# Revit family: LEGRAND_NON INTERLOCKED SOCKETS_SURFACE MOUNTED_IP44_230
name_source: partatom
category: Installations électriques
revit_build: Autodesk Revit 2018 (Build: 20170223_1515(x64)
units: mm (PartAtom-declared; Revit-internal decimal feet)

## family parameters
Conserver l'orientation des annotations = Non
Cote de connecteur circulaire = Utiliser le diamètre
Couper avec des vides une fois chargée = Non
Hôte = Face
Partagée = Non
Point de calcul de pièce = Non
Type d'élément = Normal

## types (19) — shared parameters
Description = international standard socket for flush or surface mounting with accessory allows the connection of power devices
Dia bouchon = 50 mm  [stored 0.164042 ft]
Elévation par défaut = 1000 mm  [stored 3.28084 ft]
Fabricant = Legrand
Flush E or Surface mounting S = flush and surface mounting
General Conditions of Use = https://export.legrand.com
Maximum installation temperature = 40°C
Maximum use temperature = 100°C
Minimum installation temperature = -20°C
Minimum use temperature = -50°C
RAY BOUCHON = 25 mm  [stored 0.082021 ft]
Ray = 25 mm  [stored 0.082021 ft]
Standard IEC or NFC = IEC
Tension V = 230 V  50/60 Hz blue
characteristic color = blue
connecting type = screw terminals
protection class IP = IP44

## per-type parameters (varying)
| type | Modèle | Number of poles | Position of earth h | depth for flush mounting mm | depth mm | h1 | halogen free | height mm | horizontal fixing distance mm | intensity A | material of box | resistance to chocks IK | vertical fixing distance mm | width mm |
| panel mounting socket Hypra   IP44   16 A   200/250 V   2P+E   plast surface box for passage wiring | 052022 | 3 | 6 | 75 mm | 115 mm | 109 mm | Oui | 182 mm | 52 mm | 16 A | plastic | 09 | 60 mm | 86 mm |
| panel mounting socket Hypra   IP44   16 A   200/250 V   3P+E   plast surface box for passage wiring | 052023 | 4 | 9 | 77 mm | 117 mm | 127 mm | Oui | 212 mm | 60 mm | 16 A | plastic | 09 | 70 mm | 100 mm  [stored 0.328084 ft] |
| panel mounting socket Hypra   IP44   16 A   200/250 V   3P+N+E   plast surface box for passage wiring | 052024 | 5 | 9 | 77 mm | 121 mm | 127 mm | Oui | 212 mm | 60 mm | 16 A | plastic | 09 | 70 mm | 100 mm  [stored 0.328084 ft] |
| panel mounting socket Hypra   IP44   16 A   200/250 V   2P+E   métal surface mounting | 052032 | 3 | 6 | 58 mm | 98 mm | 64 mm | Oui | 106 mm | 52 mm | 16 A | metal | 10 | 60 mm | 74 mm |
| panel mounting socket Hypra   IP44   16 A   200/250 V   3P+N+E   métal surface mounting | 052034 | 5 | 9 | 60 mm | 104 mm | 73 mm | Oui | 122 mm  [stored 0.400262 ft] | 60 mm | 16 A | metal | 10 | 70 mm | 96 mm |
| panel mounting socket Hypra   IP44   32 A   200/250 V   2P+E   plast surface box for passage wiring | 052718 | 3 | 6 | 90 mm | 143 mm | 97 mm | Oui | 162 mm | 70 mm | 32 A | plastic | 09 | 70 mm | 102 mm |
| panel mounting socket Hypra   IP44   32 A   200/250 V  3P+E   plast surface box for passage wiring | 052719 | 4 | 9 | 90 mm | 143 mm | 97 mm | Oui | 162 mm | 70 mm | 32 A | plastic | 09 | 70 mm | 102 mm |
| panel mounting socket Hypra   IP44   32 A   200/250 V   3P+N+E   plast surface box for passage wiring | 052720 | 5 | 9 | 90 mm | 146 mm  [stored 0.479003 ft] | 97 mm | Oui | 162 mm | 70 mm | 32 A | plastic | 09 | 70 mm | 102 mm |
| panel mounting socket Hypra   IP44   32 A   200/250 V  2P+E   métal surface mounting | 052732 | 5 | 9 | 90 mm | 143 mm | 97 mm | Oui | 162 mm | 70 mm | 32 A | metal | 09 | 80 mm | 102 mm |
| panel mounting socket Hypra   IP44   32 A   200/250 V   3P+E  métal surface mounting | 052733 | 4 | 9 | 90 mm | 143 mm | 97 mm | Oui | 162 mm | 70 mm | 32 A | metal | 10 | 80 mm | 102 mm |
| panel mounting socket Hypra   IP44   63 A   200/250 V   2P+E   plast surface box for passage wiring | 053622 | 3 | 6 | 150 mm | 220 mm | 180 mm  [stored 0.590551 ft] | Non | 300 mm | 77 mm | 63 A | plastic | 09 | 85 mm | 170 mm |
| panel mounting socket Hypra   IP44   63 A   200/250 V   3P+E   plast surface box for passage wiring | 053623 | 4 | 9 | 150 mm | 220 mm | 180 mm  [stored 0.590551 ft] | Non | 300 mm | 77 mm | 63 A | plastic | 09 | 85 mm | 170 mm |
| panel mounting socket Hypra   IP44   16 A   200/250 V   3P+E   métal surface mounting | 052033 | 4 | 9 | 60 mm | 100 mm  [stored 0.328084 ft] | 73 mm | Oui | 122 mm  [stored 0.400262 ft] | 60 mm | 16 A | metal | 10 | 70 mm | 96 mm |
| panel mounting socket Hypra   IP44   16 A   200/250 V   2P+E   plast surface mounting | 052022 | 3 | 6 | 58 mm | 98 mm | 64 mm | Oui | 106 mm | 52 mm | 16 A | plastic | 09 | 60 mm | 74 mm |
| panel mounting socket Hypra   IP44   16 A   200/250 V   3P+E   plast surface mounting | 052023 | 4 | 9 | 60 mm | 100 mm  [stored 0.328084 ft] | 73 mm | Oui | 122 mm  [stored 0.400262 ft] | 60 mm | 16 A | plastic | 09 | 70 mm | 96 mm |
| panel mounting socket Hypra   IP44   16 A   200/250 V   3P+N+E   plast surface mounting | 052024 | 5 | 9 | 60 mm | 104 mm | 73 mm | Oui | 122 mm  [stored 0.400262 ft] | 60 mm | 16 A | plastic | 09 | 70 mm | 96 mm |
| panel mounting socket Hypra   IP44   32 A   200/250 V   2P+E   plast surface mounting | 052718 | 3 | 6 | 90 mm | 143 mm | 97 mm | Oui | 162 mm | 70 mm | 32 A | plastic | 09 | 70 mm | 102 mm |
| panel mounting socket Hypra   IP44   32 A   200/250 V  3P+E   plast surface mounting | 052719 | 4 | 9 | 90 mm | 143 mm | 97 mm | Oui | 162 mm | 70 mm | 32 A | plastic | 09 | 70 mm | 102 mm |
| panel mounting socket Hypra   IP44   32 A   200/250 V   3P+N+E   plast surface mounting | 052720 | 5 | 9 | 90 mm | 146 mm  [stored 0.479003 ft] | 97 mm | Oui | 162 mm | 70 mm | 32 A | plastic | 09 | 70 mm | 102 mm |

note: [stored X ft] marks values corroborated as IEEE doubles in the binary element streams (Revit-internal decimal feet)
